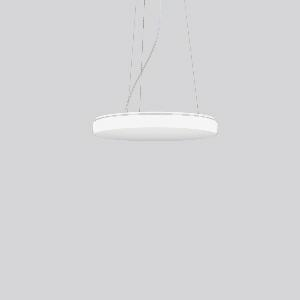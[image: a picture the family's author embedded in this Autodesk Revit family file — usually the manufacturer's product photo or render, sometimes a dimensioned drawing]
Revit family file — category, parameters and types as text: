
# Revit family: flat_polymero_kreis_slim_312091_002_3_ad95
name_source: partatom
category: Lighting Fixtures
units: mm (PartAtom-declared; Revit-internal decimal feet)

## family parameters
Cut with Voids When Loaded = No
Host = Face
Light Source = No
Part Type = Normal
Room Calculation Point = No
Round Connector Dimension = Use Diameter
Shared = No

## types (1)
- FLAT POLYMERO KREIS SLIM (1 x LED Modul 840, 3400 lm, 4000)
    Apparent Load = 28 VA
    CIE Flux Codes = 42 72 91 82 100
    Color Rendering = 80
    Color Temperature = 4000
    Default Elevation = 1800 mm
    Description = Series: FLAT POLYMERO KREIS SLIM
Decorative round LED pendant luminaire. Base and canopy: metal, powder-coated, white. Canopy Ø 205 mm, h 35 mm. Diffuser made of non-yellowing plastic (PMMA), opal. Diffuser fastening: patented push system. Homogeneous and smooth light distribution. Suitable for pendant. 3-point steel cable suspension, steplessly adjustable. Special lengths available on request. 
Colour: white
Diameter: 515 mm
Height: 69 mm
Suspension length: 350-1300 mm
Lamp: LED
Socket: without socket
Colour temperature: 4000K
Colour rendering index (CRI): 83
System power: 28 W
Rated luminous flux: 3400 lm
Luminous efficiency: 121 lm/W
Control gear: AC Strom, dim.Ph.an-/abschnitt
Protection class: I
Type of protection: IP 40
    Height = 69 mm
    Lamp = 1 x LED Modul 840
    Lamp Light Flux = 3400 lm
    Lamp count = 1
    Length = 515 mm
    Lifetime = 50000 h
    Luminous efficacy = 121 lm/W
    Manufacturer = RZB
    ModVariant = No
    Model = 312091.002.3
    Mounting Place = Ceiling
    Mounting Type = Pendant
    Number of Poles = 1
    OnlyDefault = Yes
    Power Factor = 1
    Product Name = FLAT POLYMERO KREIS SLIM
    Product group = Pendant luminaires
    ProductGroupID = 902
    Protection Class = Protection class I
    Protection Degree = IP 40
    RLX_Detail_Level = 1
    RLX_Emergency_Light_Flux = 0 lm
    RLX_Emergency_Type = 0
    RLX_Emergency_Type_DB = No
    RlxData = <blob elided: 42017 chars, md5=c8baeadd>
    Socket = socket
    Standby Power = 0 W
    System Light Flux = 3400 lm
    System Power = 28 W
    Type Comments = Product without accessories
    Type Image = 312091.002.jpg
    URL = http://relux.com
    VarID = ---
    Voltage = 230 V
    Voltage Range = 220-240 V
    Weight = 0.00 kg
    Width = 0 mm  [stored 0 ft]

note: [stored X ft] marks values corroborated as IEEE doubles in the binary element streams (Revit-internal decimal feet)

## geometry (parser evidence)
native form markers: Blend x4, Sweep x14
no freeform markers — native parametric forms only
